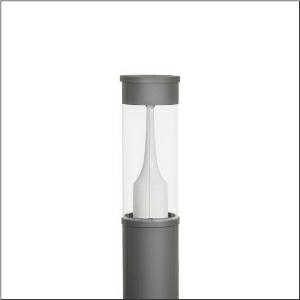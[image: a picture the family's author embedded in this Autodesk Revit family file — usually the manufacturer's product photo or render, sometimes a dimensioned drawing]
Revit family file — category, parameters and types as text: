
# Revit family: city-light_120_iq___pl1_2s_5xa5285cf14h_ce3b
name_source: partatom
category: Lighting Fixtures
units: mm (PartAtom-declared; Revit-internal decimal feet)

## family parameters
Cut with Voids When Loaded = No
Host = Face
Light Source = No
Part Type = Normal
Room Calculation Point = No
Round Connector Dimension = Use Diameter
Shared = No

## types (1)
- --- (1 x LED, 2970 lm, 23.9 W, 2200K)
    Apparent Load = 24 VA
    CIE Flux Codes = 23 62 94 96 100
    Color Rendering = 70
    Color Temperature = 2200K
    Default Elevation = 1800 mm
    Description = City-Light 120 iQ, bollard luminaire, Module 540 iQ-SR, primary light control with 3 zone facetted reflector, of plastic, silver coated, highly specular, structured, primary optical cover: cover, of PMMA, transparent, partly coated, light distribution: PL1.2s, primary light characteristic: symmetric, LED, High Power LED, rated luminous flux: 2.970lm, luminous efficacy: 124lm/W, light colour: 722, colour temperature: 2200K, control gear: iQ Street-Remote, control: pre-setting: logarithmic dimming characteristic, Street-Remote, Auto-Match, Temp-Guard, Lumen-Switch, Night-Set, Smart-Wire, Light-Fading, Desk-Remote (wireless, voltage-free reading and setting of iQ features in the workshop via application-optimized NFC function/RFID function), optimised constant luminous flux control (CLO 2.0), with terminal, 6-pole, max. 2.5mm², mains connection: 230..240V, AC, 50/60Hz, start of lifetime: 24W, end of service life: 26W, reduction: 12W, luminaire housing, cylindrical, of extruded aluminium section, coated, Siteco® metallic grey (DB 702S), length: 1.200mm, diameter: 200mm, Module 540 iQ-SR, traffic white (RAL 9016), equipment: standard, protection rating (complete): IP54, insulation class (complete): insulation class II (safety insulation), certification: CE, ENEC, VDE, packaging unit: 1 piece

Light Distribution: PL1.2s
    Height = 500 mm
    Lamp = 1 x LED
    Lamp Light Flux = 2970 lm
    Lamp Power = 23.9 W
    Lamp count = 1
    Length = 200 mm  [stored 0.656168 ft]
    Luminous efficacy = 124 lm/W
    Manufacturer = Siteco
    ModVariant = No
    Model = 5XA5285CF14H
    Mounting Place = Floor
    Mounting Type = Freestanding
    Number of Poles = 1
    OnlyDefault = Yes
    Power Factor = 1
    Product Name = City-Light 120 iQ | PL1.2s
    Product group = bollard luminaire
    ProductGroupID = 1304
    Protection Class = Protection class II
    Protection Degree = IP 54
    RLX_Detail_Level = 1
    RLX_Emergency_Light_Flux = 0 lm
    RLX_Emergency_Type = 0
    RLX_Emergency_Type_DB = No
    RlxData = <blob elided: 22477 chars, md5=f1a0988e>
    Socket = socket
    Standby Power = 0 W
    System Light Flux = 2970 lm
    System Power = 24 W
    Type Comments = factory setting: luminous flux: 100 % | dim-lin: 254 | 499 mA
    Type Image = l_1006922.jpg
    URL = http://relux.com
    VarID = @adj_145230
    Voltage = 0 V
    Weight = 0.00 kg
    Width = 0 mm  [stored 0 ft]

note: [stored X ft] marks values corroborated as IEEE doubles in the binary element streams (Revit-internal decimal feet)

## geometry (parser evidence)
native form markers: Blend x4, Sweep x11
no freeform markers — native parametric forms only
